# Revit family: Guard Pro 150E
name_source: partatom
category: Wyposażenie mechaniczne
revit_build: Autodesk Revit 2018 (Build: 20170927_1515(x64)
units: mm (PartAtom-declared; Revit-internal decimal feet)

## family parameters
Klasyfikacja = Brak
Oparty na płaszczyźnie roboczej = Nie
Punkt obliczania pomieszczeń = Nie
Tnij formami wycięć po wczytaniu = Nie
Typ części = Normalny
Współdzielony = Nie
Wymiar okrągłego złącza = Użyj średnicy
Zawsze pionowo = Tak

## types (1)
- Guard Pro 150E
    Autor = www.archispace.pl
    Fan3 = Nie
    Model = Guard Pro 150W
    Opis = Промышленная воздушно-тепловая завеса
    Producent = SONNIGER Polska Sp. z o.o. Sp. k.
    Диаметры патрубков = 19.1
    Длина завесы = 1500 mm
    Класс защиты = IP54
    Максимальная высота двери = 8 mm  [stored 0.0262467 ft]
    Максимальный расход воздуха = 6700 m³/h
    Масса = 45.00 kg
    Мощность электродвигателя = 500 W
    Напряжение питания = 230 V
    Напряжение питания нагревателя = 400 V
    Потребление тока = 17 A
    высота вентилятора 1 = 412 mm  [stored 1.35171 ft]
    высота вентилятора 2 = 1088 mm
    двигатель потребление тока = 2 A
    материал = Powder lak coated Steel

note: [stored X ft] marks values corroborated as IEEE doubles in the binary element streams (Revit-internal decimal feet)
